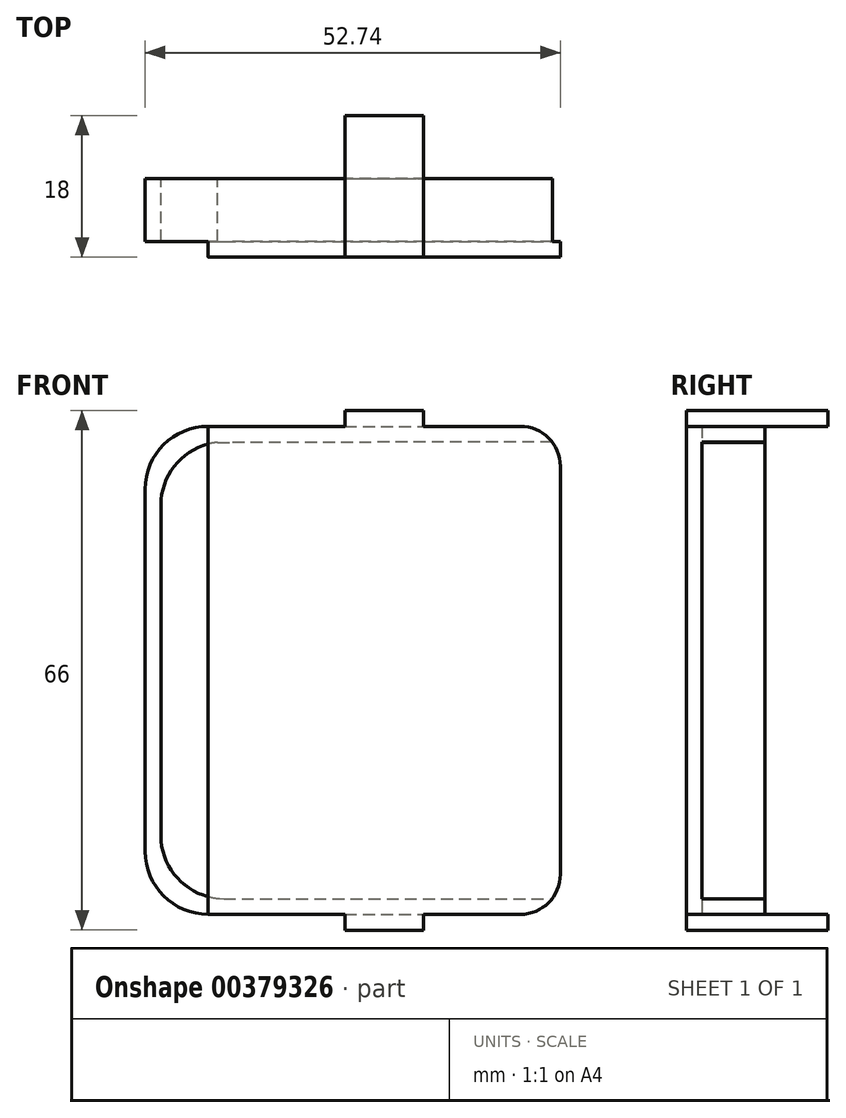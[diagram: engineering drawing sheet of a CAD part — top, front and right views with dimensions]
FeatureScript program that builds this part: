
annotation { "Feature Type Name" : "Feature", "Feature Type Description" : "" }
export const myFeature = defineFeature(function(context is Context, id is Id, definition is map)
    precondition{}
    {
        {
            var Q0;
            Q0=qCreatedBy(makeId("Front.planeOp"),FACE);
            var sketch = newSketch(context, id + "F0", { "sketchPlane" : qUnion([Q0])});
            skLineSegment(sketch, "E0.top", {"start": v(-5.34, -32.1) * mm, "end": v(37.4, -32.1) * mm});
            skLineSegment(sketch, "E0.left", {"start": v(-13.34, 17.9) * mm, "end": v(-13.34, -24.1) * mm});
            skArc(sketch, "E1.filletArc", {"start": v(-13.34, -24.1) * mm, "mid": v(-11, -29.75) * mm, "end": v(-5.34, -32.1) * mm});
            skLineSegment(sketch, "E2.top", {"start": v(-7.34, -34.1) * mm, "end": v(-5.34, -34.1) * mm});
            skLineSegment(sketch, "E2.left", {"start": v(-15.34, -24.1) * mm, "end": v(-15.34, -26.1) * mm});
            skArc(sketch, "E3.filletArc", {"start": v(-15.34, -26.1) * mm, "mid": v(-13, -31.75) * mm, "end": v(-7.34, -34.1) * mm});
            skArc(sketch, "E4.filletArc", {"start": v(-6.1, 25.87) * mm, "mid": v(-11.27, 23.29) * mm, "end": v(-13.34, 17.9) * mm});
            skLineSegment(sketch, "E5", {"start": v(0.28, 27.88) * mm, "end": v(0.28, 27.9) * mm});
            skLineSegment(sketch, "E6", {"start": v(-15.34, -24.1) * mm, "end": v(-15.34, 17.9) * mm});
            skLineSegment(sketch, "E7", {"start": v(-5.34, -34.1) * mm, "end": v(37.4, -34.1) * mm});
            skLineSegment(sketch, "E8", {"start": v(-15.34, 17.9) * mm, "end": v(-15.34, 19.92) * mm});
            skArc(sketch, "E9.filletArc", {"start": v(-7.34, 27.9) * mm, "mid": v(-13, 25.57) * mm, "end": v(-15.34, 19.92) * mm});
            skLineSegment(sketch, "E10", {"start": v(-6.1, 25.87) * mm, "end": v(-4.6, 25.87) * mm});
            skLineSegment(sketch, "E11", {"start": v(-4.6, 27.9) * mm, "end": v(-7.34, 27.9) * mm});
            skLineSegment(sketch, "E12.left", {"start": v(-15.34, 17.9) * mm, "end": v(-15.34, -26.1) * mm});
            skLineSegment(sketch, "E13", {"start": v(37.4, -32.1) * mm, "end": v(37.4, -34.1) * mm});
            skLineSegment(sketch, "E14", {"start": v(-4.6, 27.9) * mm, "end": v(37.4, 27.9) * mm});
            skLineSegment(sketch, "E15", {"start": v(37.4, 27.9) * mm, "end": v(37.4, 25.9) * mm});
            skLineSegment(sketch, "E16", {"start": v(37.4, 25.9) * mm, "end": v(-4.6, 25.87) * mm});
            skSolve(sketch);
        }
        {
            var Q0;
            Q0=makeQuery(id+"F0.imprint","IMPRINT",FACE,{"disambiguationData":[TD([[makeQuery(id+"F0.imprint","IMPRINT",EDGE,{"derivedFrom":sQuery(id+"F0.wireOp",EDGE,"E0.top")}),-1.0]])]});
            extrude(context, id + "F1", {"entities" : qUnion([Q0]), "depth" : 8 * mm, "offsetDistance" : 25.4 * mm});
        }
        {
            var Q0;
            Q0=makeQuery(id+"F1.opExtrude","CAP_FACE",FACE,{"disambiguationData":[OSD([sQuery(id+"F0.wireOp",EDGE,"E0.top"),sQuery(id+"F0.wireOp",EDGE,"E0.left"),sQuery(id+"F0.wireOp",EDGE,"E1.filletArc"),sQuery(id+"F0.wireOp",EDGE,"E2.top"),sQuery(id+"F0.wireOp",EDGE,"E3.filletArc"),sQuery(id+"F0.wireOp",EDGE,"E4.filletArc"),sQuery(id+"F0.wireOp",EDGE,"E7"),sQuery(id+"F0.wireOp",EDGE,"E8"),sQuery(id+"F0.wireOp",EDGE,"E9.filletArc"),sQuery(id+"F0.wireOp",EDGE,"E10"),sQuery(id+"F0.wireOp",EDGE,"E11"),sQuery(id+"F0.wireOp",EDGE,"E12.left"),sQuery(id+"F0.wireOp",EDGE,"E13"),sQuery(id+"F0.wireOp",EDGE,"E14"),sQuery(id+"F0.wireOp",EDGE,"E15"),sQuery(id+"F0.wireOp",EDGE,"E16")])],"isStart":false});
            var sketch = newSketch(context, id + "F2", { "sketchPlane" : qUnion([Q0])});
            skLineSegment(sketch, "E17.bottom", {"start": v(37.4, 27.9) * mm, "end": v(-7.34, 27.9) * mm});
            skLineSegment(sketch, "E17.top", {"start": v(37.4, -34.1) * mm, "end": v(-7.34, -34.1) * mm});
            skLineSegment(sketch, "E17.left", {"start": v(37.4, 27.9) * mm, "end": v(37.4, -34.1) * mm});
            skLineSegment(sketch, "E17.right", {"start": v(-7.34, 27.9) * mm, "end": v(-7.34, -34.1) * mm});
            skSolve(sketch);
        }
        {
            var Q0;
            {var subQ0=makeQuery(id+"F1.opExtrude","CAP_EDGE",EDGE,{"disambiguationData":[OSD([sQuery(id+"F0.wireOp",EDGE,"E10")])],"isStart":false});Q0=makeQuery(id+"F2.imprint","IMPRINT",FACE,{"disambiguationData":[TD([[makeQuery(id+"F2.imprint","IMPRINT",EDGE,{"derivedFrom":subQ0}),-1.0]])]});}
            var Q1;
            {var subQ9=makeQuery(id+"F1.opExtrude","CAP_EDGE",EDGE,{"disambiguationData":[OSD([sQuery(id+"F0.wireOp",EDGE,"E10")])],"isStart":false});Q1=makeQuery(id+"F2.imprint","IMPRINT",FACE,{"disambiguationData":[TD([[makeQuery(id+"F2.imprint","IMPRINT",EDGE,{"derivedFrom":subQ9}),1.0]])]});}
            var Q2;
            {var subQ6=sQuery(id+"F2.wireOp",EDGE,"E17.top");Q2=makeQuery(id+"F2.imprint","IMPRINT",FACE,{"disambiguationData":[TD([[makeQuery(id+"F2.imprint","IMPRINT",EDGE,{"derivedFrom":subQ6}),1.0]])]});}
            extrude(context, id + "F3", {"entities" : qUnion([Q0, Q1, Q2]), "operationType" : NewBodyOperationType.ADD, "depth" : 2 * mm, "offsetDistance" : 25.4 * mm});
        }
        {
            var Q0;
            Q0=makeQuery(id+"F3.boolean.opBoolean","MERGE",FACE,{"derivedFrom":[makeQuery(id+"F1.opExtrude","SWEPT_FACE",FACE,{"disambiguationData":[OSD([sQuery(id+"F0.wireOp",EDGE,"E2.top"),sQuery(id+"F0.wireOp",EDGE,"E7")])]}),makeQuery(id+"F3.opExtrude","SWEPT_FACE",FACE,{"disambiguationData":[OSD([sQuery(id+"F2.wireOp",EDGE,"E17.top")])]})]});
            var sketch = newSketch(context, id + "F4", { "sketchPlane" : qUnion([Q0])});
            skLineSegment(sketch, "E18", {"start": v(15.03, 0) * mm, "end": v(15.03, 10) * mm});
            skLineSegment(sketch, "E19.bottom", {"start": v(10.03, 10) * mm, "end": v(20.03, 10) * mm});
            skLineSegment(sketch, "E19.top", {"start": v(10.03, -8) * mm, "end": v(20.03, -8) * mm});
            skLineSegment(sketch, "E19.left", {"start": v(10.03, 10) * mm, "end": v(10.03, -8) * mm});
            skLineSegment(sketch, "E19.right", {"start": v(20.03, 10) * mm, "end": v(20.03, -8) * mm});
            skPoint(sketch, "E19.middle", {"position": v(15.03, 1) * mm});
            skSolve(sketch);
        }
        {
            var Q0;
            {var subQ0=sQuery(id+"F2.wireOp",EDGE,"E17.bottom");Q0=makeQuery(id+"F3.boolean.opBoolean","MERGE",FACE,{"derivedFrom":[makeQuery(id+"F1.opExtrude","SWEPT_FACE",FACE,{"disambiguationData":[OSD([sQuery(id+"F0.wireOp",EDGE,"E11"),sQuery(id+"F0.wireOp",EDGE,"E14")])]}),makeQuery(id+"F3.opExtrude","SWEPT_FACE",FACE,{"disambiguationData":[OSD([subQ0]),TDD([makeQuery(id+"F2.imprint","IMPRINT",EDGE,{"disambiguationData":[TD([[makeQuery(id+"F2.imprint","INTERSECT",VERTEX,{"derivedFrom":[subQ0,sQuery(id+"F2.wireOp",EDGE,"E17.left")]}),1.0]])],"derivedFrom":subQ0})])]})]});}
            var sketch = newSketch(context, id + "F5", { "sketchPlane" : qUnion([Q0])});
            skLineSegment(sketch, "E20", {"start": v(15.03, 0) * mm, "end": v(15.03, -10) * mm});
            skLineSegment(sketch, "E21.bottom", {"start": v(20.03, -10) * mm, "end": v(10.03, -10) * mm});
            skLineSegment(sketch, "E21.top", {"start": v(20.03, 8) * mm, "end": v(10.03, 8) * mm});
            skLineSegment(sketch, "E21.left", {"start": v(20.03, -10) * mm, "end": v(20.03, 8) * mm});
            skLineSegment(sketch, "E21.right", {"start": v(10.03, -10) * mm, "end": v(10.03, 8) * mm});
            skPoint(sketch, "E21.middle", {"position": v(15.03, -1) * mm});
            skSolve(sketch);
        }
        {
            var Q0;
            {var subQ4=sQuery(id+"F5.wireOp",EDGE,"E21.top");Q0=makeQuery(id+"F5.imprint","IMPRINT",FACE,{"disambiguationData":[TD([[makeQuery(id+"F5.imprint","IMPRINT",EDGE,{"derivedFrom":subQ4}),1.0]])]});}
            var Q1;
            {var subQ0=sQuery(id+"F5.wireOp",EDGE,"E20");Q1=makeQuery(id+"F5.imprint","IMPRINT",FACE,{"disambiguationData":[TD([[makeQuery(id+"F5.imprint","IMPRINT",EDGE,{"derivedFrom":subQ0}),-1.0]])]});}
            var Q2;
            {var subQ0=sQuery(id+"F5.wireOp",EDGE,"E20");Q2=makeQuery(id+"F5.imprint","IMPRINT",FACE,{"disambiguationData":[TD([[makeQuery(id+"F5.imprint","IMPRINT",EDGE,{"derivedFrom":subQ0}),1.0]])]});}
            extrude(context, id + "F6", {"entities" : qUnion([Q0, Q1, Q2]), "operationType" : NewBodyOperationType.ADD, "depth" : 2 * mm, "offsetDistance" : 25.4 * mm});
        }
        {
            var Q0;
            {var subQ4=sQuery(id+"F4.wireOp",EDGE,"E19.top");Q0=makeQuery(id+"F4.imprint","IMPRINT",FACE,{"disambiguationData":[TD([[makeQuery(id+"F4.imprint","IMPRINT",EDGE,{"derivedFrom":subQ4}),1.0]])]});}
            var Q1;
            {var subQ0=sQuery(id+"F4.wireOp",EDGE,"E18");Q1=makeQuery(id+"F4.imprint","IMPRINT",FACE,{"disambiguationData":[TD([[makeQuery(id+"F4.imprint","IMPRINT",EDGE,{"derivedFrom":subQ0}),-1.0]])]});}
            var Q2;
            {var subQ0=sQuery(id+"F4.wireOp",EDGE,"E18");Q2=makeQuery(id+"F4.imprint","IMPRINT",FACE,{"disambiguationData":[TD([[makeQuery(id+"F4.imprint","IMPRINT",EDGE,{"derivedFrom":subQ0}),1.0]])]});}
            extrude(context, id + "F7", {"entities" : qUnion([Q0, Q1, Q2]), "operationType" : NewBodyOperationType.ADD, "depth" : 2 * mm, "offsetDistance" : 25.4 * mm});
        }
        {
            var Q0;
            Q0=makeQuery(id+"F3.boolean.opBoolean","MERGE",EDGE,{"derivedFrom":[makeQuery(id+"F1.opExtrude","SWEPT_EDGE",EDGE,{"disambiguationData":[OSD([sQuery(id+"F0.wireOp",EDGE,"E14"),sQuery(id+"F0.wireOp",EDGE,"E15")])]}),makeQuery(id+"F3.opExtrude","SWEPT_EDGE",EDGE,{"disambiguationData":[OSD([sQuery(id+"F2.wireOp",EDGE,"E17.bottom"),sQuery(id+"F2.wireOp",EDGE,"E17.left")])]})]});
            var Q1;
            Q1=makeQuery(id+"F1.opExtrude","SWEPT_EDGE",EDGE,{"disambiguationData":[OSD([sQuery(id+"F0.wireOp",EDGE,"E7"),sQuery(id+"F0.wireOp",EDGE,"E13")])]});
            fillet(context, id + "F8", {"entities" : qUnion([Q0, Q1]), "radius" : 5.08 * mm, "tangentPropagation" : true, "allowEdgeOverflow" : false});
        }
    });
